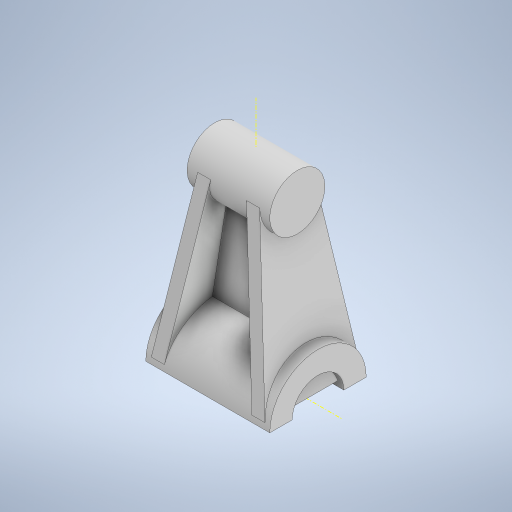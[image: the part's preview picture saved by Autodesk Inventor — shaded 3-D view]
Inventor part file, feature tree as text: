
AUTODESK INVENTOR PART (.ipt)
format: ipt  version: 2023 (Build 270158000, 158)  size: 332,288 bytes
history: native  units: mm
features: sketch x6, extrude x5, other x2, mirror x1
ambient origin geometry x8: Origin, YZ Plane, XZ Plane, XY Plane, X Axis, Y Axis, Z Axis, Center Point
bodies: Solido1 (feature_tree)
feature tree (14):
  sketch  "Schizzo1"
  extrude  "Estrusione1"  Depth=20.0mm
  extrude  "Estrusione2"  Depth=15.0mm
  sketch  "Schizzo3"
  other  "Piano di lavoro2"
  sketch  "Schizzo4"
  extrude  "Estrusione4"  Depth=96.0mm
  mirror  "Specchio1"
  sketch  "Schizzo8"
  extrude  "Estrusione5"  Depth=28.0mm
  extrude  "Estrusione6"  Depth=32.0mm
  sketch  "Schizzo9"
  sketch  "Schizzo6"
  other  "Linea chiusa proiettata1"
